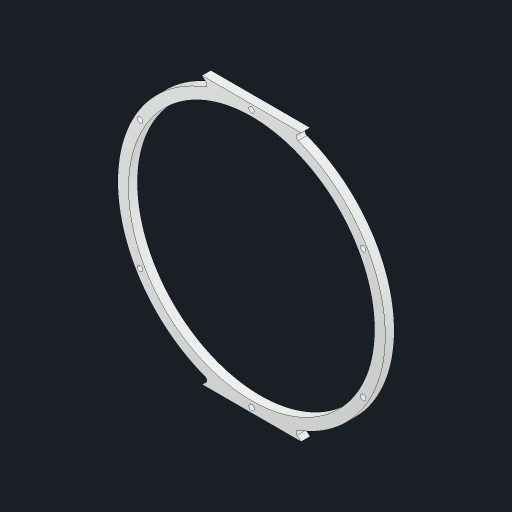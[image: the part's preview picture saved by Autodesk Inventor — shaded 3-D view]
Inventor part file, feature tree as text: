
AUTODESK INVENTOR PART (.ipt)
format: ipt  version: 2023.2 (Build 272271030, 271C)  size: 150,528 bytes
history: native  units: mm
features: extrude x4, sketch x3, mirror x2, fillet x1, pattern_circular x1
ambient origin geometry x8: Origin, YZ Plane, XZ Plane, XY Plane, X Axis, Y Axis, Z Axis, Center Point
bodies: Solid1 (feature_tree)
feature tree (11):
  sketch  "Sketch1"  dims[d0=138.0mm d1=150.0mm]
  extrude  "Extrusion1"  Depth=150.0mm
  extrude  "Extrusion2"  Depth=1.6mm
  mirror  "Mirror1"
  mirror  "Mirror2"
  extrude  "Extrusion3"  Depth=5.0mm TaperAngle=0.0deg
  extrude  "Extrusion4"  Depth=5.0mm TaperAngle=0.0deg
  fillet  "Fillet1"  Radius=3.0mm
  pattern_circular  "Circular Pattern1"  [2 undecoded]
  sketch  "Sketch2"  dims[d2=5.0mm d3=1.6mm]
  sketch  "Sketch3"  dims[d4=20.0mm d6=360.0deg d8=5.0mm d9=0.0mm d10=5.0mm d11=0.0mm d12=3.0mm d15=5.0mm d16=0.0mm d17=5.0mm d18=0.0mm d19=4.0mm d20=60.0mm d21=360.0deg d23=5.5mm]
note: 2 required parameter values undecoded (feature->parameter linkage not recoverable at this tier; creation-order binding heuristic only, values carry confidence <= 0.55)
